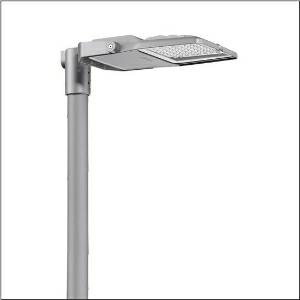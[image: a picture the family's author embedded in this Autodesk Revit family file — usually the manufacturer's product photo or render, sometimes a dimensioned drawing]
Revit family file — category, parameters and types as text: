
# Revit family: floodlight_fl_21_mini___pl43_5xa7771b2a3a_4fcf
name_source: partatom
category: Lighting Fixtures
units: mm (PartAtom-declared; Revit-internal decimal feet)

## family parameters
Cut with Voids When Loaded = No
Host = Face
Light Source = No
Part Type = Normal
Room Calculation Point = No
Round Connector Dimension = Use Diameter
Shared = No

## types (1)
- --- (1 x LED, 6400 lm, 45.5 W, 3000K)
    Apparent Load = 46 VA
    CIE Flux Codes = 27 78 99 100 100
    Color Rendering = 70
    Color Temperature = 3000K
    Default Elevation = 1800 mm
    Description = Floodlight FL 21 mini, floodlight, primary light control with lens, of PMMA, primary optical cover: protective disc, of toughened safety glass, transparent, light distribution: PL43, light emission: direct distribution, installation type: surface-mounted, LED, High Power LED, rated luminous flux: 6.400lm, luminous efficacy: 141lm/W, light colour: 730, colour temperature: 3000K, control gear: ECG iQ, control: Auto-Match, Temp-Guard, Lumen-Switch, Night-Set, Smart-Wire, Light-Fading, Desk-Remote (wireless, voltage-free reading and setting of iQ features in the workshop via application-optimized NFC function/RFID function), optimised constant luminous flux control (CLO 2.0), with terminal, 6-pole, mains connection: 220..240V, AC, 50/60Hz, start of lifetime: 46W, end of lifetime: 48W, reduction: 22W, luminaire housing, of diecast aluminium, powder-coated, Siteco® metallic grey (DB 702S), corrosivity category C5 according to DIN EN ISO 12944, mast bracket, of steel, galvanised, powder-coated, Siteco® metallic grey (DB 702S), protection rating (complete): IP66, insulation class (complete): insulation class II (safety insulation), certification: CE, ENEC, VDE, protection symbol: D, impact resistance: IK08, permissible operating ambient temperature: -40..+40°C, permissible operating ambient temperature for outdoor applications: -40..+50°C, standard: DIN EN 12944, packaging unit: 1 piece

Light Distribution: PL43
    Height = 70 mm
    Lamp = 1 x LED
    Lamp Light Flux = 6400 lm
    Lamp Power = 45.5 W
    Lamp count = 1
    Length = 485 mm
    Luminous efficacy = 141 lm/W
    Manufacturer = Siteco
    ModVariant = No
    Model = 5XA7771B2A3A
    Number of Poles = 1
    OnlyDefault = Yes
    Power Factor = 1
    Product Name = Floodlight FL 21 mini | PL43
    Product group = floodlight | pylon top
    ProductGroupID = 6101
    Protection Class = Protection class II
    Protection Degree = IP 66
    RLX_Detail_Level = 1
    RlxData = <blob elided: 100865 chars, md5=aaf7f5e8>
    Socket = socket
    Standby Power = 0 W
    System Light Flux = 6400 lm
    System Power = 46 W
    Type Comments = factory setting: luminous flux: 100 % | dim-lin: 254 | 463 mA
    Type Image = l_1007125.jpg
    URL = http://relux.com
    VarID = @adj_074193
    Voltage = 0 V
    Weight = 0.00 kg
    Width = 337 mm

## geometry (parser evidence)
native form markers: Blend x4, Sweep x12
no freeform markers — native parametric forms only
